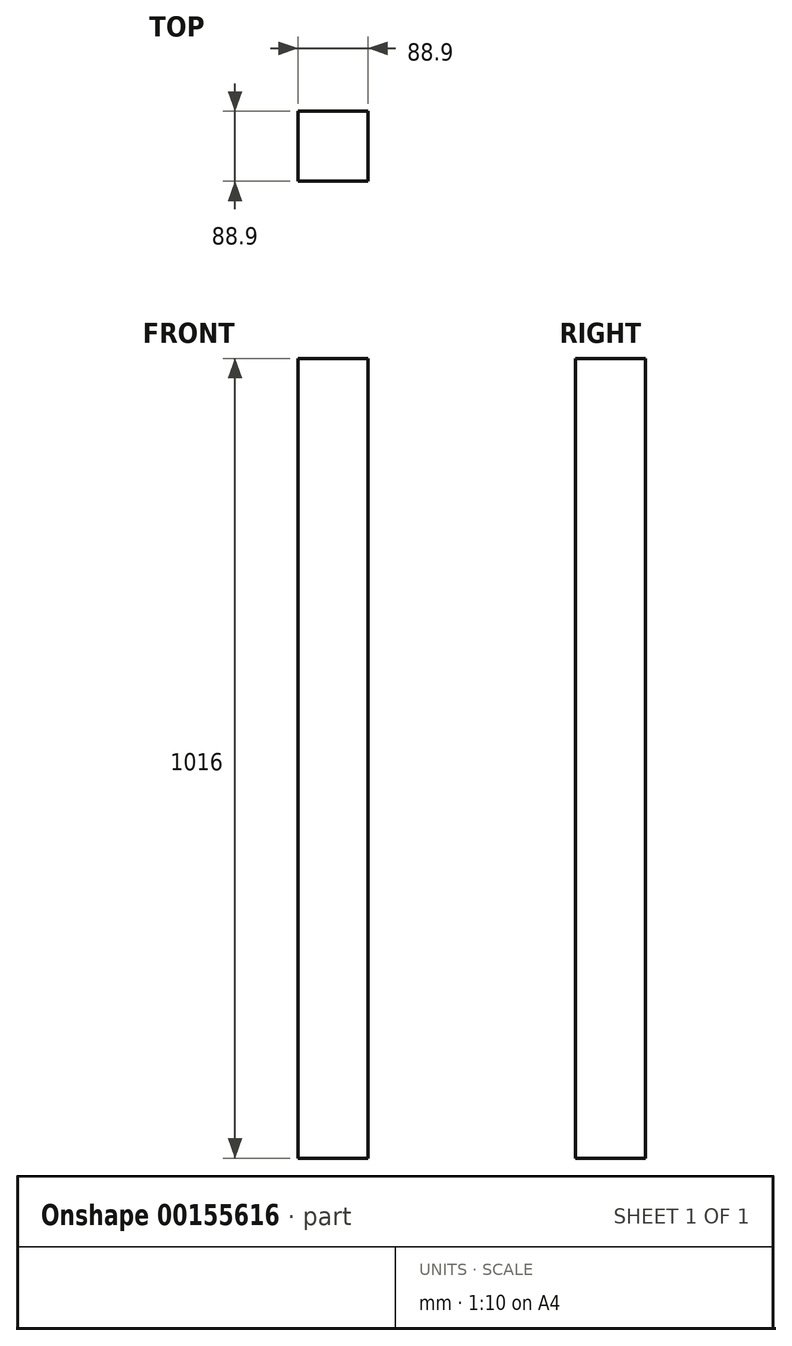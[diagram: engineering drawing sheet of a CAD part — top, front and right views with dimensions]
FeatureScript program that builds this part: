
annotation { "Feature Type Name" : "Feature", "Feature Type Description" : "" }
export const myFeature = defineFeature(function(context is Context, id is Id, definition is map)
    precondition{}
    {
        {
            var Q0;
            Q0=qCreatedBy(makeId("Top.planeOp"),FACE);
            var sketch = newSketch(context, id + "F0", { "sketchPlane" : qUnion([Q0])});
            skLineSegment(sketch, "E0.bottom", {"start": v(-44.45, 44.45) * mm, "end": v(44.45, 44.45) * mm});
            skLineSegment(sketch, "E0.top", {"start": v(-44.45, -44.45) * mm, "end": v(44.45, -44.45) * mm});
            skLineSegment(sketch, "E0.left", {"start": v(-44.45, 44.45) * mm, "end": v(-44.45, -44.45) * mm});
            skLineSegment(sketch, "E0.right", {"start": v(44.45, 44.45) * mm, "end": v(44.45, -44.45) * mm});
            skPoint(sketch, "E0.middle", {"position": v(0, 0) * mm});
            skSolve(sketch);
        }
        {
            var Q0;
            Q0=makeQuery(id+"F0.imprint","IMPRINT",FACE,{"disambiguationData":[TD([[makeQuery(id+"F0.imprint","IMPRINT",EDGE,{"derivedFrom":sQuery(id+"F0.wireOp",EDGE,"E0.bottom")}),-1.0]])]});
            extrude(context, id + "F1", {"entities" : qUnion([Q0]), "depth" : 1016 * mm});
        }
    });
